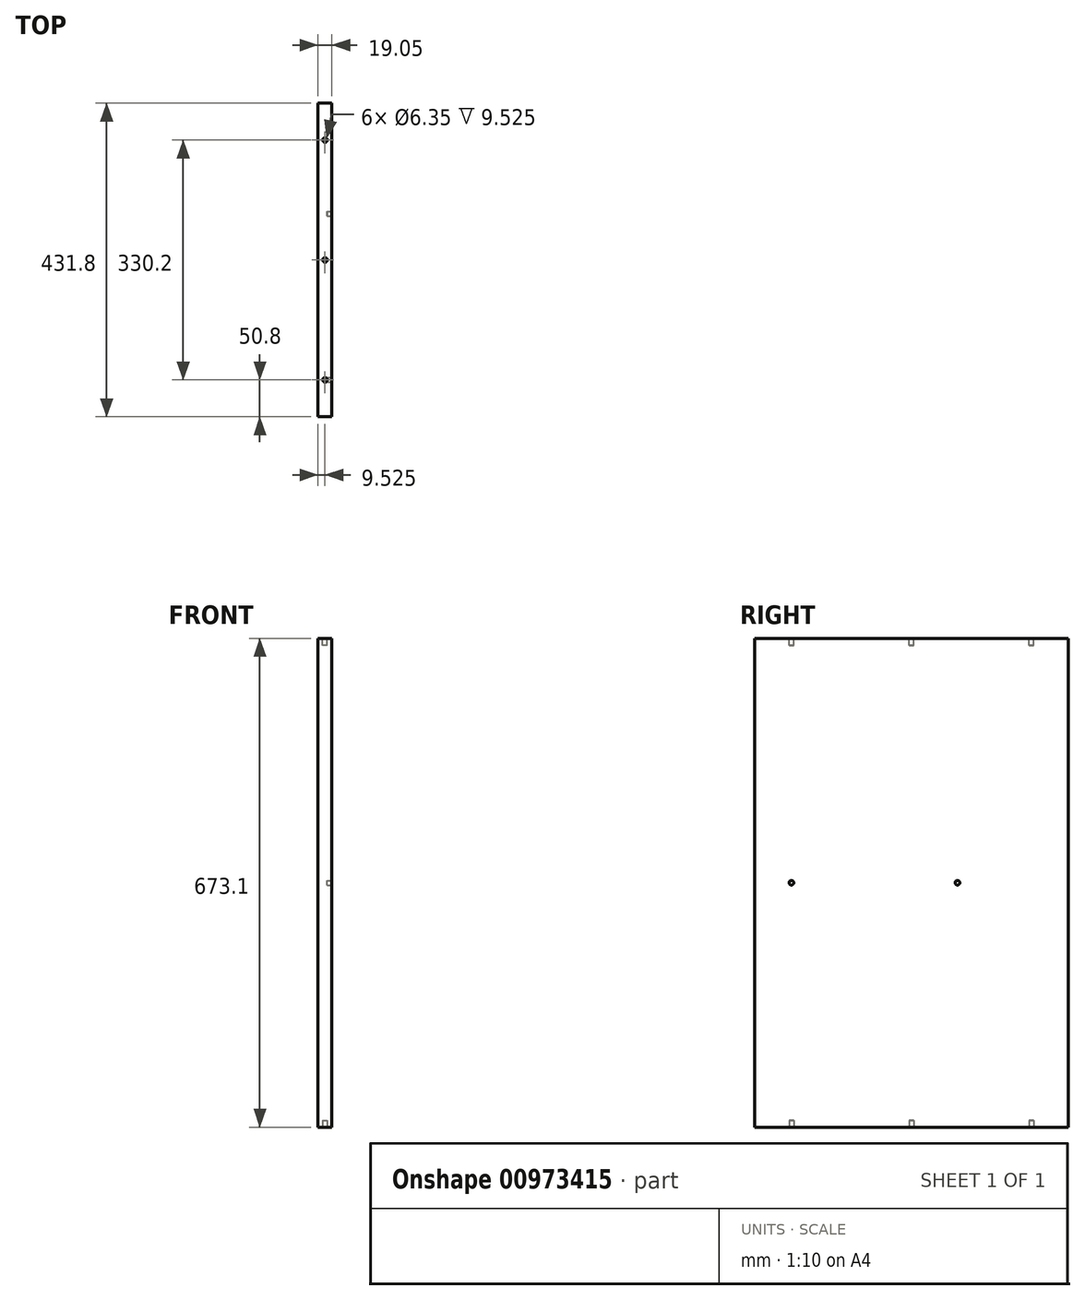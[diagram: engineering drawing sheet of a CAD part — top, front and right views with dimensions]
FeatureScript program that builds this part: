
annotation { "Feature Type Name" : "Feature", "Feature Type Description" : "" }
export const myFeature = defineFeature(function(context is Context, id is Id, definition is map)
    precondition{}
    {
        {
            var Q0;
            Q0=qCreatedBy(makeId("Top.planeOp"),FACE);
            var sketch = newSketch(context, id + "F0", { "sketchPlane" : qUnion([Q0])});
            skLineSegment(sketch, "E0.bottom", {"start": v(0, 0) * mm, "end": v(19.05, 0) * mm});
            skLineSegment(sketch, "E0.top", {"start": v(0, 431.8) * mm, "end": v(19.05, 431.8) * mm});
            skLineSegment(sketch, "E0.left", {"start": v(0, 0) * mm, "end": v(0, 431.8) * mm});
            skLineSegment(sketch, "E0.right", {"start": v(19.05, 0) * mm, "end": v(19.05, 431.8) * mm});
            skSolve(sketch);
        }
        {
            var Q0;
            Q0=makeQuery(id+"F0.imprint","IMPRINT",FACE,{"disambiguationData":[TD([[makeQuery(id+"F0.imprint","IMPRINT",EDGE,{"derivedFrom":sQuery(id+"F0.wireOp",EDGE,"E0.bottom")}),1.0]])]});
            extrude(context, id + "F1", {"entities" : qUnion([Q0]), "depth" : 673.1 * mm, "offsetDistance" : 25.4 * mm});
        }
        {
            var Q0;
            Q0=makeQuery(id+"F1.opExtrude","CAP_FACE",FACE,{"disambiguationData":[OSD([sQuery(id+"F0.wireOp",EDGE,"E0.bottom"),sQuery(id+"F0.wireOp",EDGE,"E0.top"),sQuery(id+"F0.wireOp",EDGE,"E0.left"),sQuery(id+"F0.wireOp",EDGE,"E0.right")])],"isStart":true});
            var sketch = newSketch(context, id + "F2", { "sketchPlane" : qUnion([Q0])});
            skCircle(sketch, "E1", {"center": v(9.53, -50.8) * mm, "radius": 3.18 * mm});
            skCircle(sketch, "E2", {"center": v(9.53, -215.9) * mm, "radius": 3.18 * mm});
            skCircle(sketch, "E3", {"center": v(9.53, -381) * mm, "radius": 3.18 * mm});
            skSolve(sketch);
        }
        {
            var Q0;
            Q0 = qSketchRegion(id + "F2", true);
            extrude(context, id + "F3", {"entities" : qUnion([Q0]), "operationType" : NewBodyOperationType.REMOVE, "oppositeDirection" : true, "depth" : 9.52 * mm, "offsetDistance" : 25.4 * mm});
        }
        {
            var Q0;
            Q0=makeQuery(id+"F1.opExtrude","CAP_FACE",FACE,{"disambiguationData":[OSD([sQuery(id+"F0.wireOp",EDGE,"E0.bottom"),sQuery(id+"F0.wireOp",EDGE,"E0.top"),sQuery(id+"F0.wireOp",EDGE,"E0.left"),sQuery(id+"F0.wireOp",EDGE,"E0.right")])],"isStart":false});
            var sketch = newSketch(context, id + "F4", { "sketchPlane" : qUnion([Q0])});
            skCircle(sketch, "E4", {"center": v(9.52, 381) * mm, "radius": 3.18 * mm});
            skCircle(sketch, "E5", {"center": v(9.52, 215.9) * mm, "radius": 3.18 * mm});
            skCircle(sketch, "E6", {"center": v(9.52, 50.8) * mm, "radius": 3.18 * mm});
            skSolve(sketch);
        }
        {
            var Q0;
            Q0 = qSketchRegion(id + "F4", true);
            extrude(context, id + "F5", {"entities" : qUnion([Q0]), "operationType" : NewBodyOperationType.REMOVE, "oppositeDirection" : true, "depth" : 9.52 * mm, "offsetDistance" : 25.4 * mm});
        }
        {
            var Q0;
            Q0=makeQuery(id+"F1.opExtrude","SWEPT_FACE",FACE,{"disambiguationData":[OSD([sQuery(id+"F0.wireOp",EDGE,"E0.right")])]});
            var sketch = newSketch(context, id + "F6", { "sketchPlane" : qUnion([Q0])});
            skCircle(sketch, "E7", {"center": v(50.8, 336.55) * mm, "radius": 3.18 * mm});
            skCircle(sketch, "E8", {"center": v(279.4, 336.55) * mm, "radius": 3.18 * mm});
            skSolve(sketch);
        }
        {
            var Q0;
            Q0 = qSketchRegion(id + "F6", true);
            extrude(context, id + "F7", {"entities" : qUnion([Q0]), "operationType" : NewBodyOperationType.REMOVE, "oppositeDirection" : true, "depth" : 6.35 * mm, "offsetDistance" : 25.4 * mm});
        }
    });
